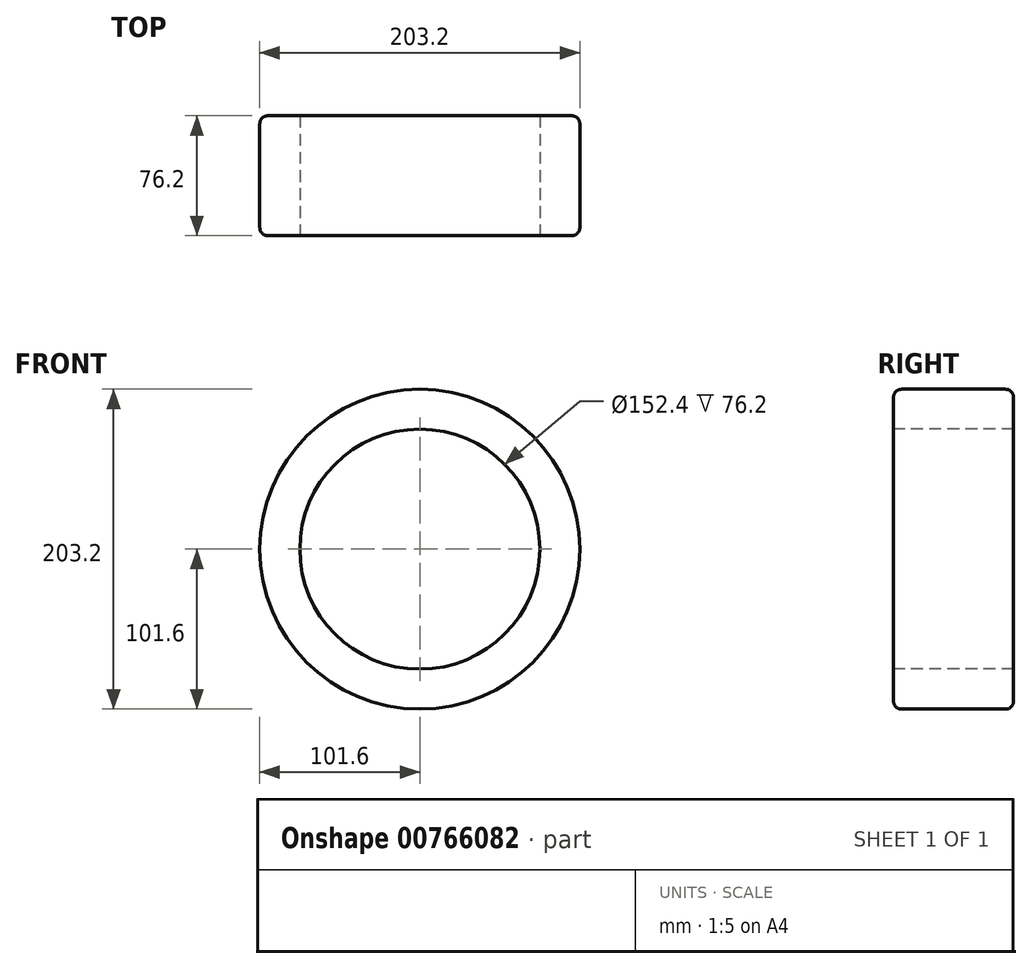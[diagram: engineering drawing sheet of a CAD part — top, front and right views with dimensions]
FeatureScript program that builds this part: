
annotation { "Feature Type Name" : "Feature", "Feature Type Description" : "" }
export const myFeature = defineFeature(function(context is Context, id is Id, definition is map)
    precondition{}
    {
        {
            var Q0;
            Q0=qCreatedBy(makeId("Front.planeOp"),FACE);
            var sketch = newSketch(context, id + "F0", { "sketchPlane" : qUnion([Q0])});
            skCircle(sketch, "E0", {"center": v(0, 0) * mm, "radius": 101.6 * mm});
            skSolve(sketch);
        }
        {
            var Q0;
            Q0=makeQuery(id+"F0.imprint","IMPRINT",FACE,{"disambiguationData":[TD([[makeQuery(id+"F0.imprint","IMPRINT",EDGE,{"derivedFrom":sQuery(id+"F0.wireOp",EDGE,"E0")}),1.0]])]});
            extrude(context, id + "F1", {"entities" : qUnion([Q0]), "depth" : 76.2 * mm, "offsetDistance" : 25.4 * mm});
        }
        {
            var Q0;
            Q0=makeQuery(id+"F1.opExtrude","CAP_FACE",FACE,{"disambiguationData":[OSD([sQuery(id+"F0.wireOp",EDGE,"E0")])],"isStart":false});
            var sketch = newSketch(context, id + "F2", { "sketchPlane" : qUnion([Q0])});
            skPoint(sketch, "E1", {"position": v(0, 101.6) * mm});
            skPoint(sketch, "E2", {"position": v(0, 0) * mm});
            skPoint(sketch, "E3", {"position": v(101.6, 0) * mm});
            skSolve(sketch);
        }
        {
            var Q0;
            Q0=sQuery(id+"F2.wireOp",VERTEX,"E2");
            var Q1;
            Q1=makeQuery(id+"F1.opExtrude","SWEPT_BODY",BODY,{"disambiguationData":[OSD([sQuery(id+"F0.wireOp",EDGE,"E0")])]});
            hole(context, id + "F3", {"style" : HoleStyle.SIMPLE, "endStyle" : HoleEndStyle.THROUGH, "holeDiameter" : 152.4 * mm, "majorDiameter" : 6.35 * mm, "isTappedThrough" : true, "tappedDepth" : 12.7 * mm, "tapClearance" : 3, "locations" : qUnion([Q0]), "scope" : qUnion([Q1])});
        }
        {
            var Q0;
            Q0=makeQuery(id+"F1.opExtrude","CAP_EDGE",EDGE,{"disambiguationData":[OSD([sQuery(id+"F0.wireOp",EDGE,"E0")])],"isStart":false});
            var Q1;
            Q1=makeQuery(id+"F1.opExtrude","CAP_EDGE",EDGE,{"disambiguationData":[OSD([sQuery(id+"F0.wireOp",EDGE,"E0")])],"isStart":true});
            var Q2;
            Q2=makeQuery(id+"F3.hole-0.boolean.opBoolean","COPY",FACE,{"derivedFrom":makeQuery(id+"F3.hole-0.opRevolve","SWEPT_FACE",FACE,{"disambiguationData":[OSD([sQuery(id+"F3.hole-0.sketch.wireOp",EDGE,"core_line_2")])]})});
            fillet(context, id + "F4", {"entities" : qUnion([Q0, Q1, Q2]), "radius" : 5.08 * mm, "tangentPropagation" : true, "allowEdgeOverflow" : false});
        }
    });
